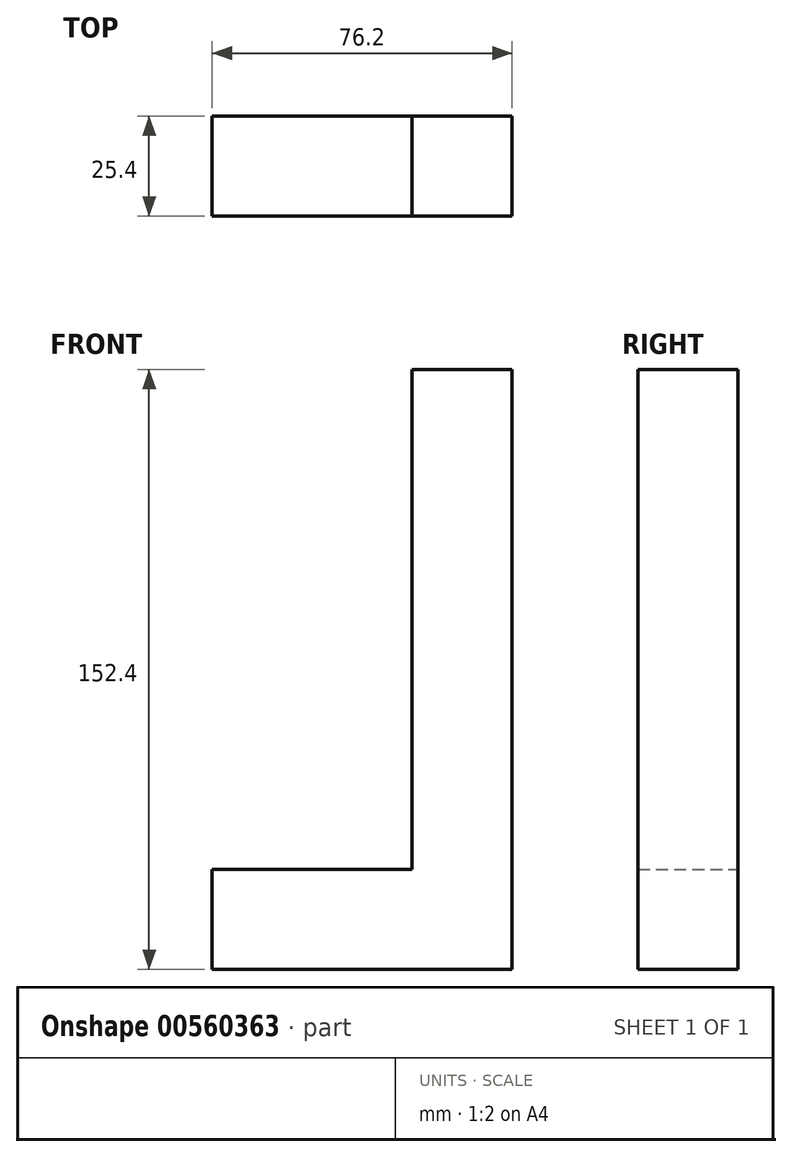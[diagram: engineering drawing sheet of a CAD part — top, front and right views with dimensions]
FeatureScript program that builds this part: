
annotation { "Feature Type Name" : "Feature", "Feature Type Description" : "" }
export const myFeature = defineFeature(function(context is Context, id is Id, definition is map)
    precondition{}
    {
        {
            var Q0;
            Q0=qCreatedBy(makeId("Front.planeOp"),FACE);
            var sketch = newSketch(context, id + "F0", { "sketchPlane" : qUnion([Q0])});
            skLineSegment(sketch, "E0", {"start": v(0, 0) * mm, "end": v(-76.2, 0) * mm});
            skLineSegment(sketch, "E1", {"start": v(-76.2, 0) * mm, "end": v(-76.2, 25.4) * mm});
            skLineSegment(sketch, "E2", {"start": v(-76.2, 25.4) * mm, "end": v(-25.4, 25.4) * mm});
            skLineSegment(sketch, "E3", {"start": v(-25.4, 25.4) * mm, "end": v(-25.4, 152.4) * mm});
            skLineSegment(sketch, "E4", {"start": v(-25.4, 152.4) * mm, "end": v(0, 152.4) * mm});
            skLineSegment(sketch, "E5", {"start": v(0, 152.4) * mm, "end": v(0, 0) * mm});
            skSolve(sketch);
        }
        {
            var Q0;
            Q0 = qSketchRegion(id + "F0", true);
            extrude(context, id + "F1", {"entities" : qUnion([Q0]), "endBound" : BoundingType.SYMMETRIC, "depth" : 25.4 * mm, "offsetDistance" : 25.4 * mm});
        }
    });
